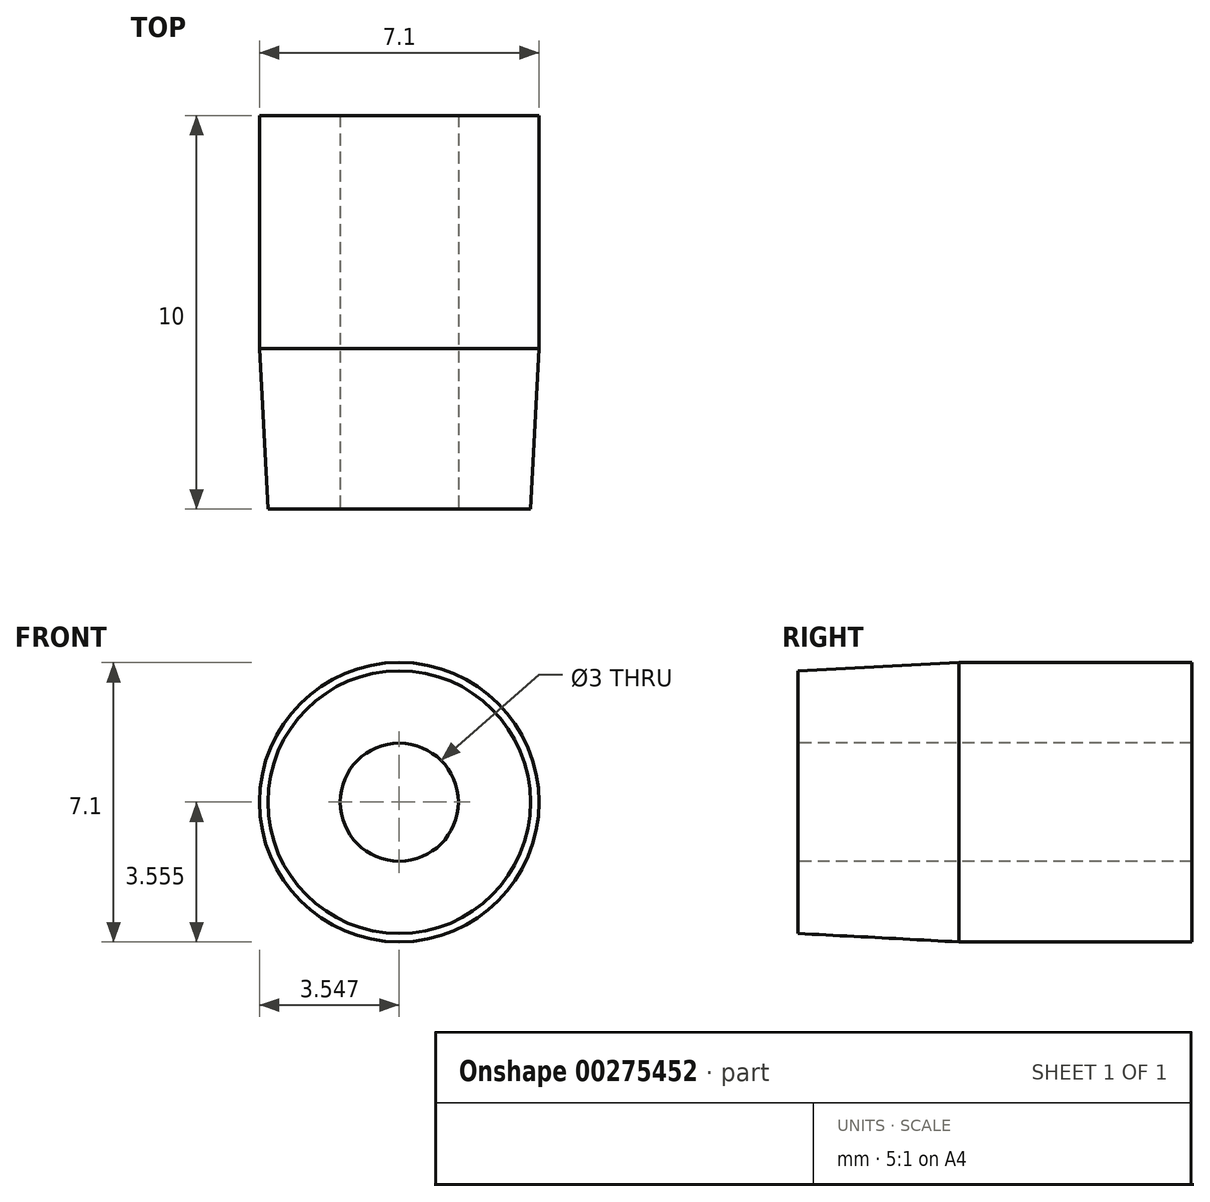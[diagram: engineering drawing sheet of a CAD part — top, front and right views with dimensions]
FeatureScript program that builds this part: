
annotation { "Feature Type Name" : "Feature", "Feature Type Description" : "" }
export const myFeature = defineFeature(function(context is Context, id is Id, definition is map)
    precondition{}
    {
        {
            var Q0;
            Q0=qCreatedBy(makeId("Front.planeOp"),FACE);
            var sketch = newSketch(context, id + "F0", { "sketchPlane" : qUnion([Q0])});
            skCircle(sketch, "E0", {"center": v(-36.08, 37.07) * mm, "radius": 3.55 * mm});
            skSolve(sketch);
        }
        {
            var Q0;
            Q0=qSketchRegion(id+"F0",true);
            extrude(context, id + "F1", {"entities" : qUnion([Q0]), "depth" : 25 * mm});
        }
        {
            var Q0;
            Q0=makeQuery(id+"F1.opExtrude","CAP_EDGE",EDGE,{"disambiguationData":[OSD([sQuery(id+"F0.wireOp",EDGE,"E0")])],"isStart":false});
            chamfer(context, id + "F2", {"entities" : qUnion([Q0]), "chamferType" : ChamferType.OFFSET_ANGLE, "width" : 1 * mm, "oppositeDirection" : false, "angle" : 87 * degree, "tangentPropagation" : true});
        }
        {
            var Q0;
            Q0=makeQuery(id+"F1.opExtrude","CAP_FACE",FACE,{"disambiguationData":[OSD([sQuery(id+"F0.wireOp",EDGE,"E0")])],"isStart":false});
            var sketch = newSketch(context, id + "F3", { "sketchPlane" : qUnion([Q0])});
            skCircle(sketch, "E1", {"center": v(-36.08, 37.07) * mm, "radius": 4.5 * mm});
            skSolve(sketch);
        }
        {
            var Q0;
            Q0=qSketchRegion(id+"F3",true);
            extrude(context, id + "F4", {"entities" : qUnion([Q0]), "operationType" : NewBodyOperationType.REMOVE, "oppositeDirection" : true, "depth" : 15 * mm});
        }
        {
            var Q0;
            Q0=makeQuery(id+"F4.boolean.opBoolean","COPY",FACE,{"derivedFrom":makeQuery(id+"F4.opExtrude","CAP_FACE",FACE,{"disambiguationData":[OSD([sQuery(id+"F3.wireOp",EDGE,"E1")])],"isStart":false})});
            var sketch = newSketch(context, id + "F5", { "sketchPlane" : qUnion([Q0])});
            skCircle(sketch, "E2", {"center": v(-36.08, 37.07) * mm, "radius": 1.5 * mm});
            skSolve(sketch);
        }
        {
            var Q0;
            Q0=qSketchRegion(id+"F5",true);
            extrude(context, id + "F6", {"entities" : qUnion([Q0]), "operationType" : NewBodyOperationType.REMOVE, "oppositeDirection" : true, "depth" : 25 * mm});
        }
    });
